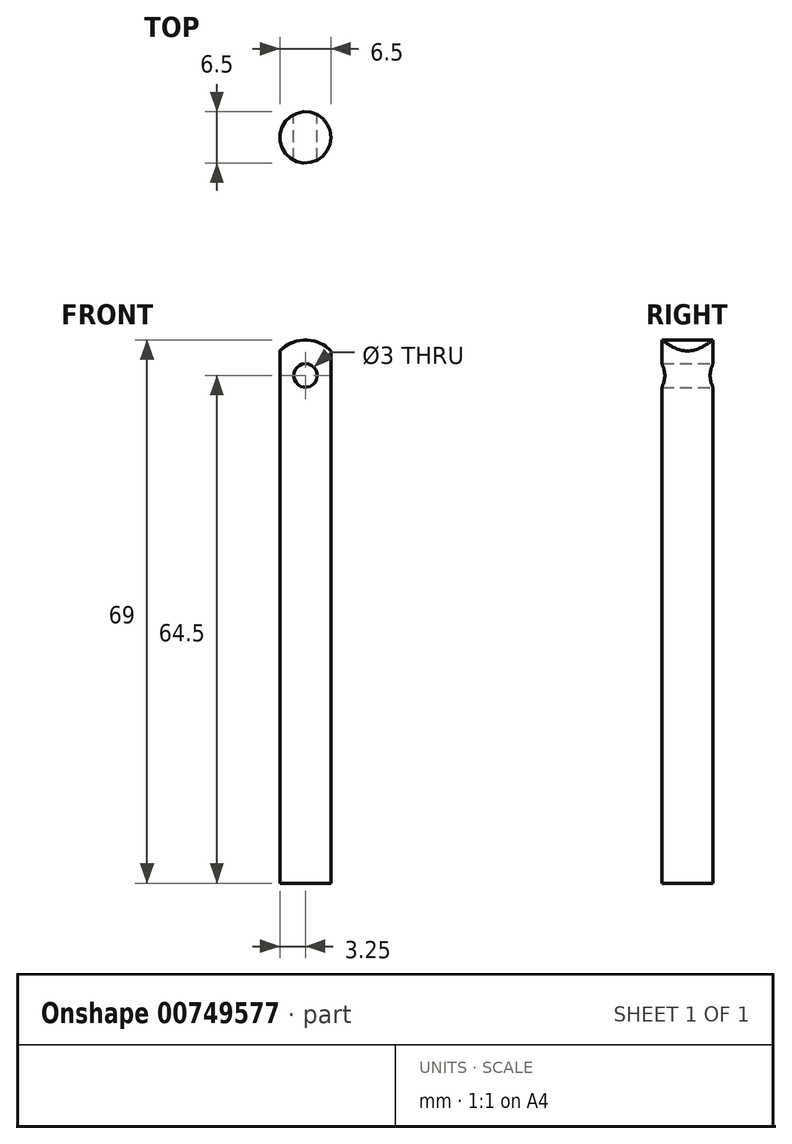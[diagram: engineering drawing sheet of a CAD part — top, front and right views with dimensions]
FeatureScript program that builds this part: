
annotation { "Feature Type Name" : "Feature", "Feature Type Description" : "" }
export const myFeature = defineFeature(function(context is Context, id is Id, definition is map)
    precondition{}
    {
        {
            var Q0;
            Q0=qCreatedBy(makeId("Top.planeOp"),FACE);
            var sketch = newSketch(context, id + "F0", { "sketchPlane" : qUnion([Q0])});
            skCircle(sketch, "E0", {"center": v(0, 0) * mm, "radius": 3.25 * mm});
            skSolve(sketch);
        }
        {
            var Q0;
            Q0=makeQuery(id+"F0.imprint","IMPRINT",FACE,{"disambiguationData":[TD([[makeQuery(id+"F0.imprint","IMPRINT",EDGE,{"derivedFrom":sQuery(id+"F0.wireOp",EDGE,"E0")}),1.0]])]});
            extrude(context, id + "F1", {"entities" : qUnion([Q0]), "oppositeDirection" : true, "depth" : 60 * mm, "offsetDistance" : 25 * mm});
        }
        {
            var Q0;
            Q0=qCreatedBy(makeId("Front.planeOp"),FACE);
            var sketch = newSketch(context, id + "F2", { "sketchPlane" : qUnion([Q0])});
            skArc(sketch, "E1", {"start": v(3.57, 1.77) * mm, "mid": v(0, 9) * mm, "end": v(-3.57, 1.77) * mm});
            skCircle(sketch, "E2", {"center": v(0, 4.5) * mm, "radius": 1.5 * mm});
            skLineSegment(sketch, "E3", {"start": v(-3.25, 0) * mm, "end": v(3.25, 0) * mm});
            skArc(sketch, "E4", {"start": v(3.57, 1.77) * mm, "mid": v(3.33, 0.9) * mm, "end": v(3.25, 0) * mm});
            skArc(sketch, "E5.MirrorCS", {"start": v(-3.57, 1.77) * mm, "mid": v(-3.33, 0.9) * mm, "end": v(-3.25, 0) * mm});
            skLineSegment(sketch, "E6", {"start": v(-3.57, 1.77) * mm, "end": v(3.57, 1.77) * mm, "construction": true});
            skSolve(sketch);
        }
        {
            var Q0;
            Q0=makeQuery(id+"F2.imprint","IMPRINT",FACE,{"disambiguationData":[TD([[makeQuery(id+"F2.imprint","IMPRINT",EDGE,{"derivedFrom":sQuery(id+"F2.wireOp",EDGE,"E1")}),1.0]])]});
            var Q1;
            Q1=makeQuery(id+"F1.opExtrude","SWEPT_FACE",FACE,{"disambiguationData":[OSD([sQuery(id+"F0.wireOp",EDGE,"E0")])]});
            extrude(context, id + "F3", {"entities" : qUnion([Q0]), "operationType" : NewBodyOperationType.ADD, "endBound" : BoundingType.UP_TO_SURFACE, "depth" : 25 * mm, "endBoundEntityFace" : qUnion([Q1]), "offsetDistance" : 25 * mm, "hasSecondDirection" : true, "secondDirectionOppositeDirection" : true, "secondDirectionDepth" : 25 * mm});
        }
    });
